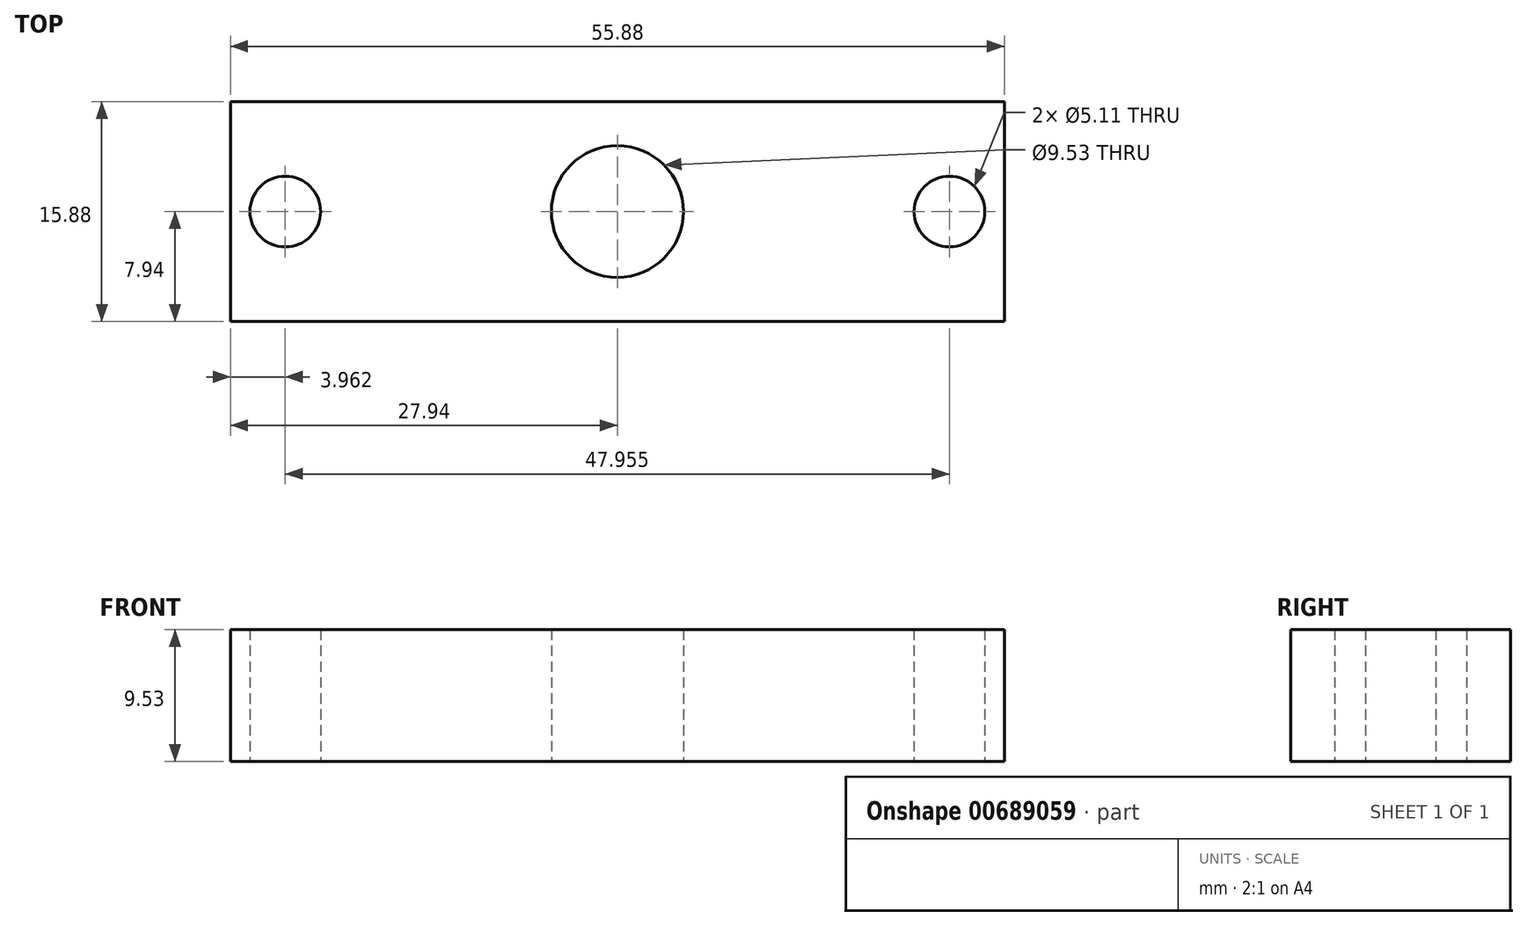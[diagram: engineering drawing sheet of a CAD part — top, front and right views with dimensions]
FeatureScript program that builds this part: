
annotation { "Feature Type Name" : "Feature", "Feature Type Description" : "" }
export const myFeature = defineFeature(function(context is Context, id is Id, definition is map)
    precondition{}
    {
        {
            var Q0;
            Q0=qCreatedBy(makeId("Top.planeOp"),FACE);
            var sketch = newSketch(context, id + "F0", { "sketchPlane" : qUnion([Q0])});
            skLineSegment(sketch, "E0.bottom", {"start": v(-27.94, 7.94) * mm, "end": v(27.94, 7.94) * mm});
            skLineSegment(sketch, "E0.top", {"start": v(-27.94, -7.94) * mm, "end": v(27.94, -7.94) * mm});
            skLineSegment(sketch, "E0.left", {"start": v(-27.94, 7.94) * mm, "end": v(-27.94, -7.94) * mm});
            skLineSegment(sketch, "E0.right", {"start": v(27.94, 7.94) * mm, "end": v(27.94, -7.94) * mm});
            skPoint(sketch, "E0.middle", {"position": v(0, 0) * mm});
            skCircle(sketch, "E1", {"center": v(0, 0) * mm, "radius": 23.98 * mm, "construction": true});
            skPoint(sketch, "E2", {"position": v(-23.98, 0) * mm});
            skPoint(sketch, "E3", {"position": v(23.98, 0) * mm});
            skSolve(sketch);
        }
        {
            var Q0;
            Q0=makeQuery(id+"F0.imprint","IMPRINT",FACE,{"disambiguationData":[TD([[makeQuery(id+"F0.imprint","IMPRINT",EDGE,{"derivedFrom":sQuery(id+"F0.wireOp",EDGE,"E0.bottom")}),-1.0]])]});
            extrude(context, id + "F1", {"entities" : qUnion([Q0]), "depth" : 9.52 * mm, "offsetDistance" : 25.4 * mm});
        }
        {
            var Q0;
            Q0=sQuery(id+"F0.wireOp",VERTEX,"E2");
            var Q1;
            Q1=sQuery(id+"F0.wireOp",VERTEX,"E3");
            var Q2;
            Q2=makeQuery(id+"F1.opExtrude","SWEPT_BODY",BODY,{"disambiguationData":[OSD([sQuery(id+"F0.wireOp",EDGE,"E0.bottom"),sQuery(id+"F0.wireOp",EDGE,"E0.top"),sQuery(id+"F0.wireOp",EDGE,"E0.left"),sQuery(id+"F0.wireOp",EDGE,"E0.right")])]});
            hole(context, id + "F2", {"style" : HoleStyle.SIMPLE, "endStyle" : HoleEndStyle.THROUGH, "oppositeDirection" : true, "standardTappedOrClearance" : lookupTablePath({ "standard" : "ANSI", "fit" : "Normal (ASME)", "size" : "#10", "type" : "Clearance" }), "standardBlindInLast" : lookupTablePath({ "fit" : "Free", "standard" : "ANSI", "size" : "#10", "type" : "Clearance" }), "holeDiameter" : 5.1 * mm, "majorDiameter" : 6.35 * mm, "isTappedThrough" : true, "tappedDepth" : 6.35 * mm, "tapClearance" : 1, "startFromSketch" : true, "locations" : qUnion([Q0, Q1]), "scope" : qUnion([Q2])});
        }
        {
            var Q0;
            Q0=sQuery(id+"F0.wireOp",VERTEX,"E0.middle");
            var Q1;
            Q1=makeQuery(id+"F1.opExtrude","SWEPT_BODY",BODY,{"disambiguationData":[OSD([sQuery(id+"F0.wireOp",EDGE,"E0.bottom"),sQuery(id+"F0.wireOp",EDGE,"E0.top"),sQuery(id+"F0.wireOp",EDGE,"E0.left"),sQuery(id+"F0.wireOp",EDGE,"E0.right")])]});
            hole(context, id + "F3", {"style" : HoleStyle.SIMPLE, "endStyle" : HoleEndStyle.THROUGH, "oppositeDirection" : true, "holeDiameter" : 9.52 * mm, "majorDiameter" : 6.35 * mm, "isTappedThrough" : true, "tappedDepth" : 6.35 * mm, "tapClearance" : 1, "startFromSketch" : true, "locations" : qUnion([Q0]), "scope" : qUnion([Q1])});
        }
    });
